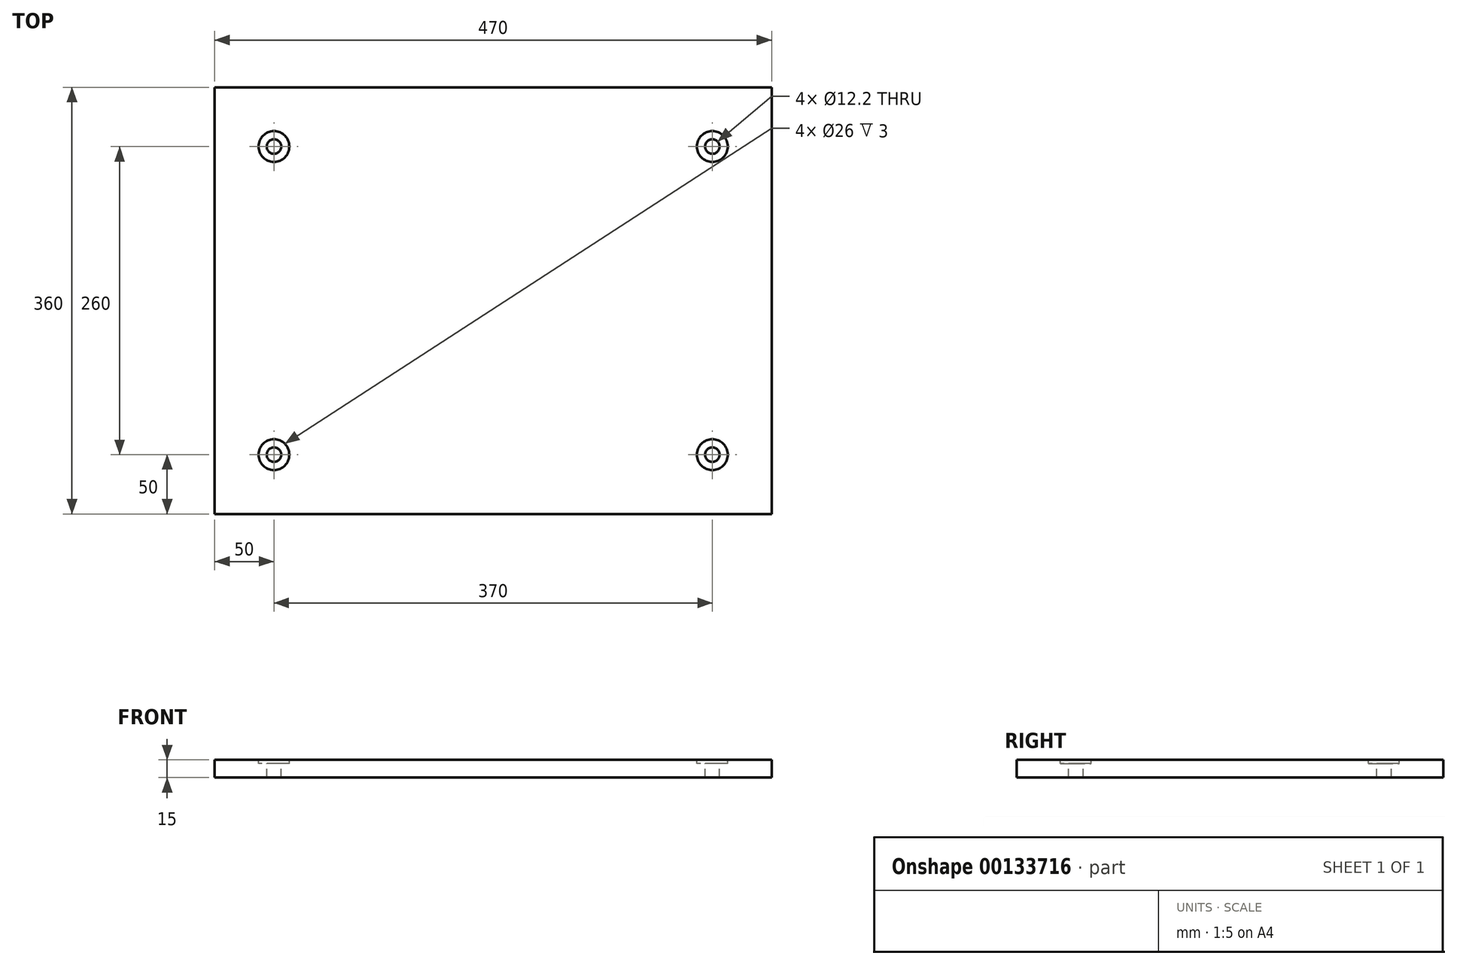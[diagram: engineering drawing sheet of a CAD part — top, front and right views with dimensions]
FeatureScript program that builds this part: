
annotation { "Feature Type Name" : "Feature", "Feature Type Description" : "" }
export const myFeature = defineFeature(function(context is Context, id is Id, definition is map)
    precondition{}
    {
        {
            var Q0;
            Q0=qCreatedBy(makeId("Top.planeOp"),FACE);
            var sketch = newSketch(context, id + "F0", { "sketchPlane" : qUnion([Q0])});
            skLineSegment(sketch, "E0.bottom", {"start": v(0, 0) * mm, "end": v(470, 0) * mm});
            skLineSegment(sketch, "E0.top", {"start": v(0, 360) * mm, "end": v(470, 360) * mm});
            skLineSegment(sketch, "E0.left", {"start": v(0, 0) * mm, "end": v(0, 360) * mm});
            skLineSegment(sketch, "E0.right", {"start": v(470, 0) * mm, "end": v(470, 360) * mm});
            skLineSegment(sketch, "E1.bottom", {"start": v(5, 5) * mm, "end": v(445, 5) * mm, "construction": true});
            skLineSegment(sketch, "E1.top", {"start": v(5, 355) * mm, "end": v(445, 355) * mm, "construction": true});
            skLineSegment(sketch, "E1.left", {"start": v(5, 5) * mm, "end": v(5, 355) * mm, "construction": true});
            skLineSegment(sketch, "E1.right", {"start": v(445, 5) * mm, "end": v(445, 355) * mm, "construction": true});
            skSolve(sketch);
        }
        {
            var Q0;
            Q0=makeQuery(id+"F0.imprint","IMPRINT",FACE,{"disambiguationData":[TD([[makeQuery(id+"F0.imprint","IMPRINT",EDGE,{"derivedFrom":sQuery(id+"F0.wireOp",EDGE,"E0.bottom")}),1.0]])]});
            extrude(context, id + "F1", {"entities" : qUnion([Q0]), "depth" : 15 * mm, "offsetDistance" : 25 * mm});
        }
        {
            var Q0;
            Q0=makeQuery(id+"F1.opExtrude","CAP_FACE",FACE,{"disambiguationData":[OSD([sQuery(id+"F0.wireOp",EDGE,"E0.bottom"),sQuery(id+"F0.wireOp",EDGE,"E0.top"),sQuery(id+"F0.wireOp",EDGE,"E0.left"),sQuery(id+"F0.wireOp",EDGE,"E0.right")])],"isStart":false});
            var sketch = newSketch(context, id + "F2", { "sketchPlane" : qUnion([Q0])});
            skPoint(sketch, "E2", {"position": v(50, 50) * mm});
            skLineSegment(sketch, "E3", {"start": v(235, 0) * mm, "end": v(235, 360) * mm, "construction": true});
            skLineSegment(sketch, "E4", {"start": v(0, 180) * mm, "end": v(470, 180) * mm, "construction": true});
            skPoint(sketch, "E4.endSnap0", {"position": v(470, 180) * mm});
            skPoint(sketch, "E5.MirrorP", {"position": v(420, 50) * mm});
            skPoint(sketch, "E6.MirrorP", {"position": v(420, 310) * mm});
            skPoint(sketch, "E7.MirrorP", {"position": v(50, 310) * mm});
            skSolve(sketch);
        }
        {
            var Q0;
            Q0=sQuery(id+"F2.wireOp",VERTEX,"E7.MirrorP");
            var Q1;
            Q1=sQuery(id+"F2.wireOp",VERTEX,"E2");
            var Q2;
            Q2=sQuery(id+"F2.wireOp",VERTEX,"E5.MirrorP");
            var Q3;
            Q3=sQuery(id+"F2.wireOp",VERTEX,"E6.MirrorP");
            var Q4;
            Q4=makeQuery(id+"F1.opExtrude","SWEPT_BODY",BODY,{"disambiguationData":[OSD([sQuery(id+"F0.wireOp",EDGE,"E0.bottom"),sQuery(id+"F0.wireOp",EDGE,"E0.top"),sQuery(id+"F0.wireOp",EDGE,"E0.left"),sQuery(id+"F0.wireOp",EDGE,"E0.right")])]});
            hole(context, id + "F3", {"style" : HoleStyle.C_BORE, "endStyle" : HoleEndStyle.BLIND, "holeDiameter" : 12.2 * mm, "cBoreDiameter" : 26 * mm, "cBoreDepth" : 3 * mm, "holeDepth" : 15 * mm, "isTappedThrough" : true, "tappedDepth" : 12 * mm, "tapClearance" : 3, "startFromSketch" : true, "locations" : qUnion([Q0, Q1, Q2, Q3]), "scope" : qUnion([Q4])});
        }
    });
